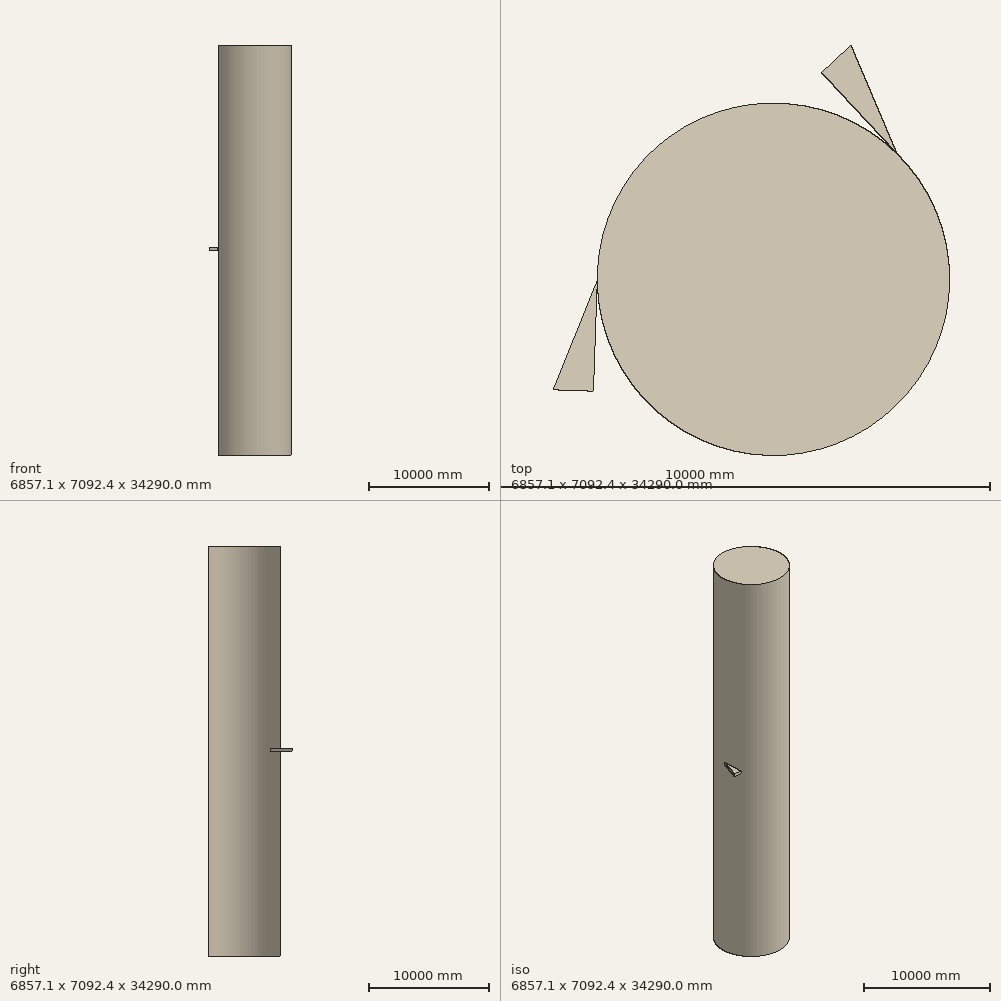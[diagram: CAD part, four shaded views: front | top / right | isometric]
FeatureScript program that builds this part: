
annotation { "Feature Type Name" : "Feature", "Feature Type Description" : "" }
export const myFeature = defineFeature(function(context is Context, id is Id, definition is map)
    precondition{}
    {
        {
            var Q0;
            Q0=qCreatedBy(makeId("Top.planeOp"),FACE);
            var sketch = newSketch(context, id + "F0", { "sketchPlane" : qUnion([Q0])});
            skCircle(sketch, "E0", {"center": v(0, 0) * mm, "radius": 3048 * mm});
            skSolve(sketch);
        }
        {
            var Q0;
            Q0 = qSketchRegion(id + "F0", true);
            extrude(context, id + "F1", {"entities" : qUnion([Q0]), "endBound" : BoundingType.SYMMETRIC, "depth" : 34290 * mm, "offsetDistance" : 25.4 * mm});
        }
        {
            var Q0;
            Q0=qCreatedBy(makeId("Top.planeOp"),FACE);
            var sketch = newSketch(context, id + "F2", { "sketchPlane" : qUnion([Q0])});
            skLineSegment(sketch, "E1", {"start": v(0, 0) * mm, "end": v(4406.08, 0) * mm, "construction": true});
            skLineSegment(sketch, "E2", {"start": v(0, 0) * mm, "end": v(-3047.88, -26.6) * mm, "construction": true});
            skLineSegment(sketch, "E3", {"start": v(-3047.88, -26.6) * mm, "end": v(-3047.88, -2062.11) * mm});
            skLineSegment(sketch, "E4", {"start": v(-3047.88, -26.6) * mm, "end": v(-3114.52, -1934.9) * mm});
            skLineSegment(sketch, "E5", {"start": v(-3114.52, -1934.9) * mm, "end": v(-3809.08, -1910.64) * mm});
            skLineSegment(sketch, "E6", {"start": v(-3809.08, -1910.64) * mm, "end": v(-3047.88, -26.6) * mm});
            skSolve(sketch);
        }
        {
            var Q0;
            Q0 = qSketchRegion(id + "F2", true);
            extrude(context, id + "F3", {"entities" : qUnion([Q0]), "depth" : 254 * mm, "offsetDistance" : 25.4 * mm});
        }
        {
            var Q0;
            Q0=makeQuery(id+"F3.opExtrude","SWEPT_BODY",BODY,{"disambiguationData":[OSD([sQuery(id+"F2.wireOp",EDGE,"E4"),sQuery(id+"F2.wireOp",EDGE,"E5"),sQuery(id+"F2.wireOp",EDGE,"E6")])]});
            var Q1;
            Q1=makeQuery(id+"F1.opExtrude","CAP_EDGE",EDGE,{"disambiguationData":[OSD([sQuery(id+"F0.wireOp",EDGE,"E0")])],"isStart":false});
            circularPattern(context, id + "F4", {"entities" : qUnion([Q0]), "axis" : qUnion([Q1]), "angle" : 135 * degree, "instanceCount" : 2, "oppositeDirection" : true});
        }
    });
